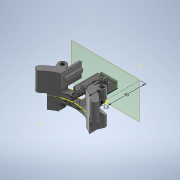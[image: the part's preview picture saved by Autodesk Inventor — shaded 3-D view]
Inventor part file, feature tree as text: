
AUTODESK INVENTOR PART (.ipt)
format: ipt  version: 2020 (Build 240168000, 168)  size: 670,720 bytes
history: native  units: mm
features: extrude x13, sketch x13, projected_geometry x10, other x3, sweep x1
ambient origin geometry x8: Origin, YZ Plane, XZ Plane, XY Plane, X Axis, Y Axis, Z Axis, Center Point
bodies: Body1 (feature_tree)
feature tree (40):
  other  "Твердое тело1"
  extrude  "Выдавливание1"  Depth=35.0mm TaperAngle=0.0deg
  sketch  "Эскиз2"
  extrude  "Выдавливание2"  Depth=4.0mm
  sweep  "Сдвиг1"
  extrude  "Выдавливание5"  Depth=8.0mm
  extrude  "Выдавливание6"  Depth=35.0mm TaperAngle=0.0deg
  extrude  "Выдавливание7"  Depth=8.5mm
  extrude  "Выдавливание8"  TaperAngle=45.0deg  [1 undecoded]
  other  "РабПлоскость1"
  extrude  "Выдавливание9"  Depth=8.5mm
  extrude  "Выдавливание10"  TaperAngle=45.0deg  [1 undecoded]
  extrude  "Выдавливание11"  TaperAngle=0.0deg  [1 undecoded]
  sketch  "Эскиз13"
  sketch  "Эскиз14"
  extrude  "Выдавливание12"  Depth=15.0mm TaperAngle=0.0deg
  extrude  "Выдавливание13"  Depth=5.0mm TaperAngle=0.0deg
  other  "РабПлоскость2"
  extrude  "Выдавливание14"  Depth=15.0mm TaperAngle=0.0deg
  extrude  "Выдавливание15"  Depth=26.0mm
  sketch  "Эскиз1"
  sketch  "Эскиз3"
  projected_geometry  "Спроецированная петля1"
  projected_geometry  "Спроецированная петля2"
  sketch  "3D эскиз1"
  sketch  "Эскиз4"
  sketch  "Эскиз6"
  projected_geometry  "Спроецированная петля4"
  sketch  "Эскиз7"
  projected_geometry  "Спроецированная петля5"
  sketch  "Эскиз9"
  projected_geometry  "Спроецированная петля7"
  sketch  "Эскиз11"
  projected_geometry  "Спроецированная петля8"
  sketch  "Эскиз12"
  projected_geometry  "Спроецированная петля9"
  projected_geometry  "Спроецированная петля10"
  sketch  "Эскиз16"
  projected_geometry  "Спроецированная петля15"
  projected_geometry  "Спроецированная петля16"
note: 3 required parameter values undecoded (feature->parameter linkage not recoverable at this tier; creation-order binding heuristic only, values carry confidence <= 0.55)
